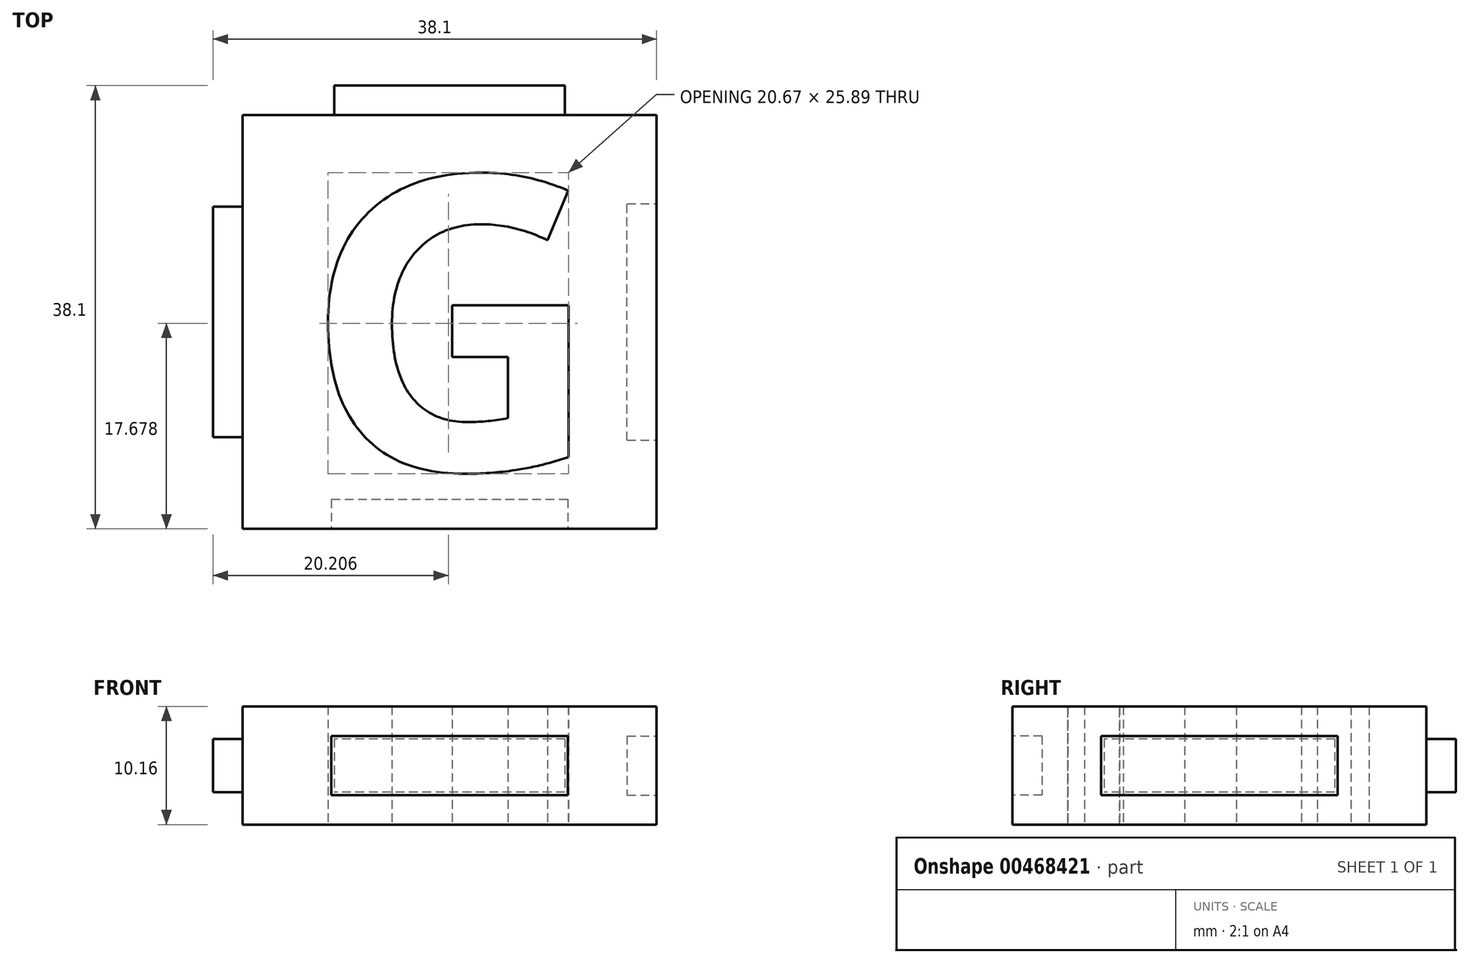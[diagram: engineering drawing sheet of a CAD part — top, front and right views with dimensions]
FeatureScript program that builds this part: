
annotation { "Feature Type Name" : "Feature", "Feature Type Description" : "" }
export const myFeature = defineFeature(function(context is Context, id is Id, definition is map)
    precondition{}
    {
        {
            var Q0;
            Q0=qCreatedBy(makeId("Top.planeOp"),FACE);
            var sketch = newSketch(context, id + "F0", { "sketchPlane" : qUnion([Q0])});
            skLineSegment(sketch, "E0.bottom", {"start": v(-17.78, 17.78) * mm, "end": v(17.78, 17.78) * mm});
            skLineSegment(sketch, "E0.top", {"start": v(-17.78, -17.78) * mm, "end": v(17.78, -17.78) * mm});
            skLineSegment(sketch, "E0.left", {"start": v(-17.78, 17.78) * mm, "end": v(-17.78, -17.78) * mm});
            skLineSegment(sketch, "E0.right", {"start": v(17.78, 17.78) * mm, "end": v(17.78, -17.78) * mm});
            skText(sketch, "E1", { "text": "G", "fontName": "OpenSans-Bold.ttf"});
            const initialGuessF0  = {"E1": [-0.0125, -0.0127, 1, 0, 0.0254]};
            skSetInitialGuess(sketch, initialGuessF0);
            skSolve(sketch);
        }
        {
            var Q0;
            Q0=qSketchRegion(id+"F0",true);
            extrude(context, id + "F1", {"entities" : qUnion([Q0]), "endBound" : BoundingType.SYMMETRIC, "depth" : 10.16 * mm});
        }
        {
            var Q0;
            Q0=makeQuery(id+"F1.opExtrude","SWEPT_FACE",FACE,{"disambiguationData":[OSD([sQuery(id+"F0.wireOp",EDGE,"E0.bottom")])]});
            var sketch = newSketch(context, id + "F2", { "sketchPlane" : qUnion([Q0])});
            skLineSegment(sketch, "E2.bottom", {"start": v(-9.9, 2.29) * mm, "end": v(9.9, 2.29) * mm});
            skLineSegment(sketch, "E2.top", {"start": v(-9.9, -2.29) * mm, "end": v(9.9, -2.29) * mm});
            skLineSegment(sketch, "E2.left", {"start": v(-9.9, 2.29) * mm, "end": v(-9.9, -2.29) * mm});
            skLineSegment(sketch, "E2.right", {"start": v(9.9, 2.29) * mm, "end": v(9.9, -2.29) * mm});
            skSolve(sketch);
        }
        {
            var Q0;
            Q0=qSketchRegion(id+"F2",true);
            extrude(context, id + "F3", {"entities" : qUnion([Q0]), "operationType" : NewBodyOperationType.ADD, "depth" : 2.54 * mm});
        }
        {
            var Q0;
            Q0=makeQuery(id+"F1.opExtrude","SWEPT_FACE",FACE,{"disambiguationData":[OSD([sQuery(id+"F0.wireOp",EDGE,"E0.left")])]});
            var sketch = newSketch(context, id + "F4", { "sketchPlane" : qUnion([Q0])});
            skLineSegment(sketch, "E3.bottom", {"start": v(-9.9, 2.29) * mm, "end": v(9.9, 2.29) * mm});
            skLineSegment(sketch, "E3.top", {"start": v(-9.9, -2.29) * mm, "end": v(9.9, -2.29) * mm});
            skLineSegment(sketch, "E3.left", {"start": v(-9.9, 2.29) * mm, "end": v(-9.9, -2.29) * mm});
            skLineSegment(sketch, "E3.right", {"start": v(9.9, 2.29) * mm, "end": v(9.9, -2.29) * mm});
            skSolve(sketch);
        }
        {
            var Q0;
            Q0=qSketchRegion(id+"F4",true);
            extrude(context, id + "F5", {"entities" : qUnion([Q0]), "operationType" : NewBodyOperationType.ADD, "depth" : 2.54 * mm});
        }
        {
            var Q0;
            Q0=makeQuery(id+"F1.opExtrude","SWEPT_FACE",FACE,{"disambiguationData":[OSD([sQuery(id+"F0.wireOp",EDGE,"E0.top")])]});
            var sketch = newSketch(context, id + "F6", { "sketchPlane" : qUnion([Q0])});
            skLineSegment(sketch, "E4.bottom", {"start": v(-10.16, 2.54) * mm, "end": v(10.16, 2.54) * mm});
            skLineSegment(sketch, "E4.top", {"start": v(-10.16, -2.54) * mm, "end": v(10.16, -2.54) * mm});
            skLineSegment(sketch, "E4.left", {"start": v(-10.16, 2.54) * mm, "end": v(-10.16, -2.54) * mm});
            skLineSegment(sketch, "E4.right", {"start": v(10.16, 2.54) * mm, "end": v(10.16, -2.54) * mm});
            skSolve(sketch);
        }
        {
            var Q0;
            Q0=qSketchRegion(id+"F6",true);
            extrude(context, id + "F7", {"entities" : qUnion([Q0]), "operationType" : NewBodyOperationType.REMOVE, "oppositeDirection" : true, "depth" : 2.54 * mm});
        }
        {
            var Q0;
            Q0=makeQuery(id+"F1.opExtrude","SWEPT_FACE",FACE,{"disambiguationData":[OSD([sQuery(id+"F0.wireOp",EDGE,"E0.right")])]});
            var sketch = newSketch(context, id + "F8", { "sketchPlane" : qUnion([Q0])});
            skLineSegment(sketch, "E5.bottom", {"start": v(-10.16, 2.54) * mm, "end": v(10.16, 2.54) * mm});
            skLineSegment(sketch, "E5.top", {"start": v(-10.16, -2.54) * mm, "end": v(10.16, -2.54) * mm});
            skLineSegment(sketch, "E5.left", {"start": v(-10.16, 2.54) * mm, "end": v(-10.16, -2.54) * mm});
            skLineSegment(sketch, "E5.right", {"start": v(10.16, 2.54) * mm, "end": v(10.16, -2.54) * mm});
            skSolve(sketch);
        }
        {
            var Q0;
            Q0=qSketchRegion(id+"F8",true);
            extrude(context, id + "F9", {"entities" : qUnion([Q0]), "operationType" : NewBodyOperationType.REMOVE, "oppositeDirection" : true, "depth" : 2.54 * mm});
        }
    });
